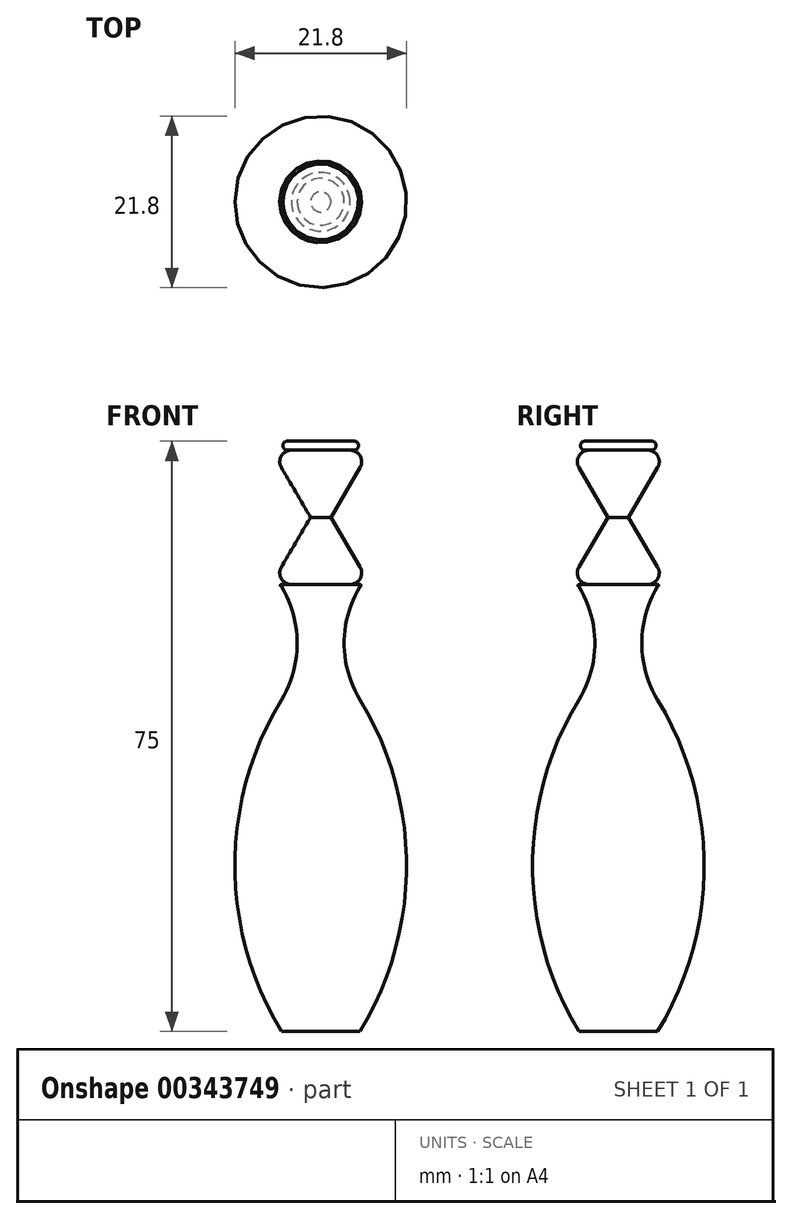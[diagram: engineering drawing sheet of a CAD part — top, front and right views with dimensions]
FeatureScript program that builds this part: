
annotation { "Feature Type Name" : "Feature", "Feature Type Description" : "" }
export const myFeature = defineFeature(function(context is Context, id is Id, definition is map)
    precondition{}
    {
        {
            var Q0;
            Q0=qCreatedBy(makeId("Front.planeOp"),FACE);
            var sketch = newSketch(context, id + "F0", { "sketchPlane" : qUnion([Q0])});
            skLineSegment(sketch, "E0", {"start": v(5, -75) * mm, "end": v(0, -75) * mm});
            skLineSegment(sketch, "E1", {"start": v(0, -75) * mm, "end": v(0, 0) * mm});
            skArc(sketch, "E2", {"start": v(5, -75) * mm, "mid": v(10.9, -53.93) * mm, "end": v(5, -32.86) * mm});
            skArc(sketch, "E3", {"start": v(5, -18.5) * mm, "mid": v(2.99, -25.67) * mm, "end": v(5, -32.86) * mm});
            skLineSegment(sketch, "E4", {"start": v(4.24, 0) * mm, "end": v(0, 0) * mm});
            skLineSegment(sketch, "E5", {"start": v(5, -18.22) * mm, "end": v(3.73, -18.22) * mm});
            skArc(sketch, "E6", {"start": v(3.73, -18.22) * mm, "mid": v(5, -17.47) * mm, "end": v(5, -15.99) * mm});
            skLineSegment(sketch, "E7", {"start": v(4.24, -1.14) * mm, "end": v(3.73, -1.14) * mm});
            skArc(sketch, "E8", {"start": v(5, -3.37) * mm, "mid": v(5, -1.88) * mm, "end": v(3.73, -1.14) * mm});
            skLineSegment(sketch, "E9", {"start": v(5, -15.99) * mm, "end": v(1.28, -9.68) * mm});
            skLineSegment(sketch, "E10", {"start": v(1.28, -9.68) * mm, "end": v(5, -3.37) * mm});
            skArc(sketch, "E11", {"start": v(4.24, -1.14) * mm, "mid": v(4.8, -0.57) * mm, "end": v(4.24, 0) * mm});
            skArc(sketch, "E12", {"start": v(5.04, -18.46) * mm, "mid": v(5.02, -18.47) * mm, "end": v(5, -18.5) * mm});
            skArc(sketch, "E13", {"start": v(5.04, -18.46) * mm, "mid": v(5.13, -18.32) * mm, "end": v(5, -18.22) * mm});
            skSolve(sketch);
        }
        {
            var Q0;
            Q0=makeQuery(id+"F0.imprint","IMPRINT",FACE,{"disambiguationData":[TD([[makeQuery(id+"F0.imprint","IMPRINT",EDGE,{"derivedFrom":sQuery(id+"F0.wireOp",EDGE,"E0")}),-1.0]])]});
            var Q1;
            Q1=sQuery(id+"F0.wireOp",EDGE,"E1");
            revolve(context, id + "F1", {"entities" : qUnion([Q0]), "axis" : qUnion([Q1]), "revolveType" : RevolveType.FULL});
        }
    });
